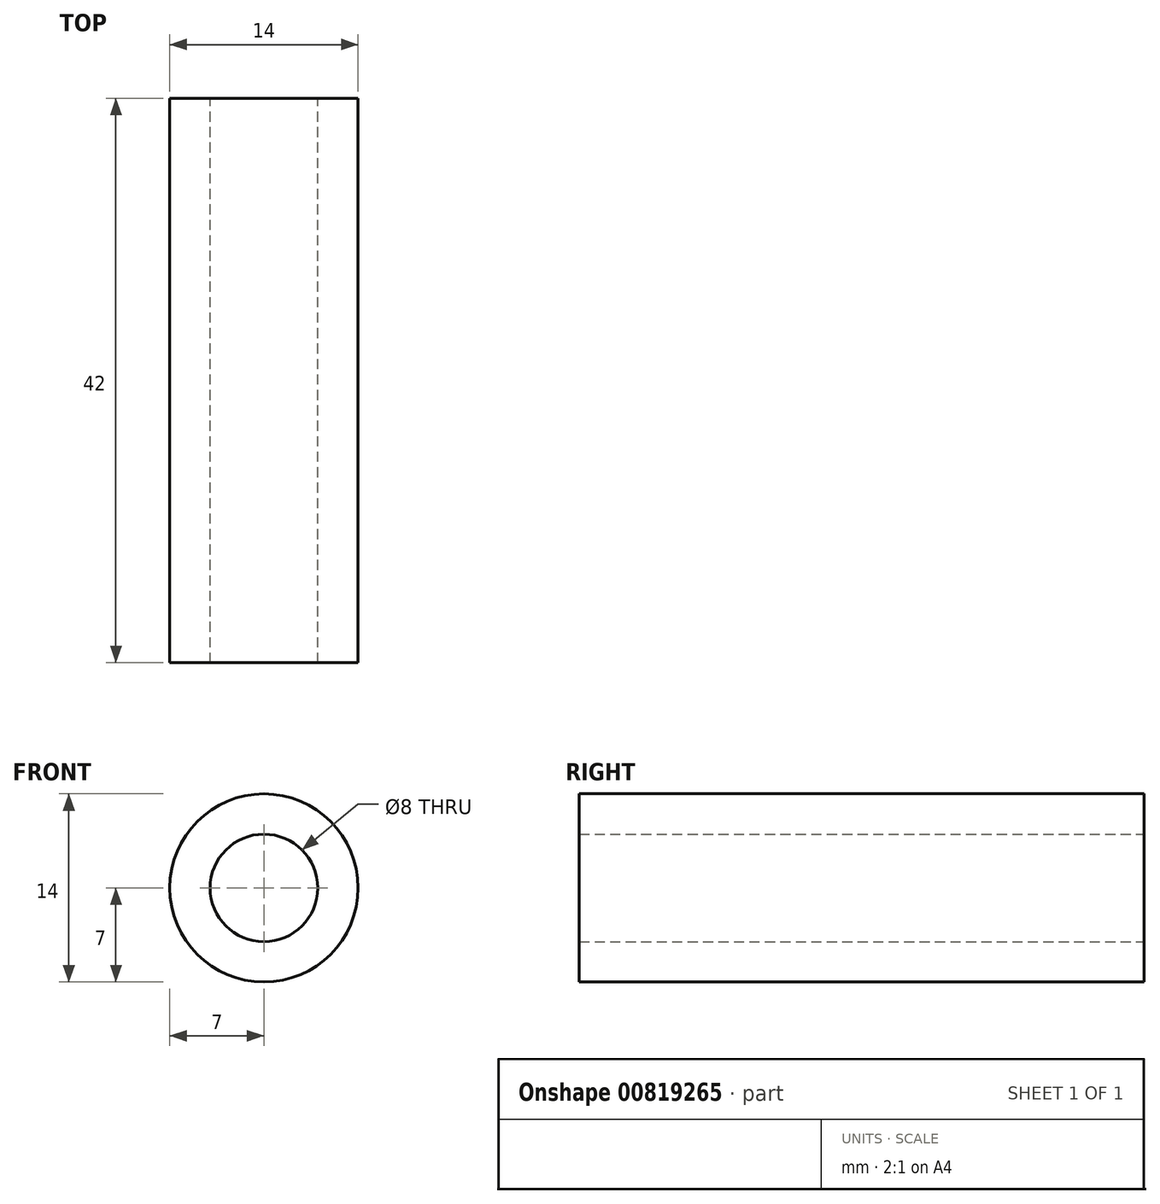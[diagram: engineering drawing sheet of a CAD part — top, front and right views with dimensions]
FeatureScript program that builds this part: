
annotation { "Feature Type Name" : "Feature", "Feature Type Description" : "" }
export const myFeature = defineFeature(function(context is Context, id is Id, definition is map)
    precondition{}
    {
        {
            var Q0;
            Q0=qCreatedBy(makeId("Front.planeOp"),FACE);
            var sketch = newSketch(context, id + "F0", { "sketchPlane" : qUnion([Q0])});
            skCircle(sketch, "E0", {"center": v(0, 0) * mm, "radius": 7 * mm});
            skCircle(sketch, "E1", {"center": v(0, 0) * mm, "radius": 4 * mm});
            skSolve(sketch);
        }
        {
            var Q0;
            Q0=makeQuery(id+"F0.imprint","IMPRINT",FACE,{"disambiguationData":[TD([[makeQuery(id+"F0.imprint","IMPRINT",EDGE,{"derivedFrom":sQuery(id+"F0.wireOp",EDGE,"E0")}),1.0]])]});
            extrude(context, id + "F1", {"entities" : qUnion([Q0]), "endBound" : BoundingType.SYMMETRIC, "depth" : 42 * mm, "offsetDistance" : 25 * mm});
        }
    });
